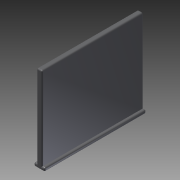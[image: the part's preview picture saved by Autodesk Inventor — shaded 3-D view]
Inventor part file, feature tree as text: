
AUTODESK INVENTOR PART (.ipt)
format: ipt  version: 2013 (Build 170138000, 138)  size: 105,472 bytes
history: native  units: in
note: dims shown in document units (in); Inventor stores cm internally (conversion verified against a paired STEP export)
features: extrude x1, fillet x1, sketch x1
ambient origin geometry x8: Origin, YZ Plane, XZ Plane, XY Plane, X Axis, Y Axis, Z Axis, Center Point
bodies: Solid1 (feature_tree)
feature tree (3):
  extrude  "Extrusion1"  Depth=0.1575in
  fillet  "Fillet1"  Radius=0.0512in
  sketch  "Sketch1"  dims[d0=1.272in d1=0.1575in d2=0.0512in d3=0.0394in d4=0.0394in d5=1.496in d6=0.0in d7=0.02in]
